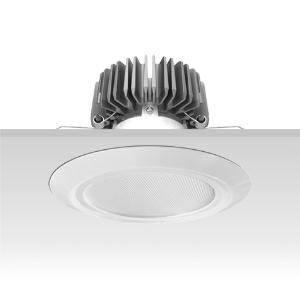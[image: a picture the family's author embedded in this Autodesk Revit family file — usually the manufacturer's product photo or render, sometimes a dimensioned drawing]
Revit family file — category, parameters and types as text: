
# Revit family: 3f_filippi_-_3f_reno_bianco_ampio_3f_filippi_-_30683_a01048_-_3f_reno_200_wh_3000-930_dali_wide___smp_wh_9ca3
name_source: partatom
category: Lighting Fixtures
units: mm (PartAtom-declared; Revit-internal decimal feet)

## family parameters
Cut with Voids When Loaded = No
Host = Face
Light Source = No
Part Type = Normal
Room Calculation Point = No
Round Connector Dimension = Use Diameter
Shared = No

## types (1)
- 3F Filippi - 3F Reno Bianco Ampio (1 x LED, 2320 lm, 37 W, 3000 K)
    Apparent Load = 37 VA
    Approval mark = CE
    CIE Flux Codes = 74 92 98 100 100
    Color Rendering = 90
    Color Temperature = 3000 K
    Control Gear = Electronic transformer
    Default Elevation = 1800 mm
    Description = ILLUMINOTECHNICAL
Luminous efficiency 100% (DLOR 100%, ULOR 0%).
Initial luminous flux of the luminaire 2320 lm.
Direct symmetric wide distribution.
Installation Interdistance Transv.D = 1.06 x hu - Long.D = 1.04 x hu.
Tabular UGR (CIE 117 - 4H-8H; S=0.25H; 70/50/20): RUG 22.5 - 22.3.
Beam angle: 70° - 69°.
Luminous efficacy 63 lm/W.
Lifetime (L90/B10): 30000 h. (tq+25°C)
Lifetime (L85/B10): 50000 h. (tq+25°C)
Lifetime (L70/B10): 80000 h. (tq+25°C)
Sudden decreased luminous flux after 50000 hours: 0% (C0).
Photobiological safety in compliance with IEC/TR 62778: RG0 risk exempt, (IEC 62471).
In compliance with IEC/EN 62722-2-1 - IEC/EN 62717 standards.

SOURCE
Compact LED module 3000/930.
Energy efficiency class (UE 2019/2020 - UE 2019/2015): E.
CIE 13.3 Colour rendering index: CRI >90 (R9 >50%).
IES TM-30 Fidelity Index: Rf = 92 Rg = 101.
CCT nominal colour temperature 3000 K.
Colour initial tolerance (MacAdam): SDCM 3.
Zhaga Book 3 compliant.

MECHANICAL
Passive heat dissipator in die-casting aluminium, oversized, for optimum thermal management of the LED module.
Parabolic element with graduated/concentric rings in white polycarbonate.
Transparent external lens with glossy and satin differentiated surfaces, with a cooling and anti-insect system in methacrylate (PMMA).
Fastening spring clips in stainless steel.
Dimensions: diameter 226 mm, height 146 mm. Weight 1.695 kg.
IP44 protection degree for exposed part, IP20 for recessed part.
Mechanical strength to impacts IK05 (0.7 joule).
Glow-wire test resistance 650°C.

ELECTRICAL
Wiring on a separate unit.
Halogen Free DALI-2 DATI (Parts 251, 252, 253), PUSH-DIM, electronic wiring 230V-50/60Hz, power factor 0.97 at full load, THD <25%, constant output current, SELV, class II, 1 driver, 1 DALI addresse.
Power of the luminaire 37 W.
ENEC - CE.
SAFE FLICKER: PstLM=<1 and SVM=<0.4 (IEC TR 61547-1 and IEC TR 63158), to ensure a more comfortable and safe light.
Luminaire compliant with EN 60598-2-22 for power supply from a centralised emergency system CPSS (Central Power Supply System), not incorporated in the luminaire - high risk areas excluded. The default power and flux are 100% in AC and 100% in DC.
Ambient temperature from 0°C to +25°C.
Temperature class T6 max 85°C.
Relative humidity UR: <85%.

INSTALLATION
Pull-up recessed fitting.
False ceiling carving: 200 mm.
All accessories dedicated to this product are available on the Catalog and on our website www.3F-Filippi.com.

ACCESSORIES
A01048 - Anti-glare microprismatic SMP diffuser in methacrylate (PMMA), locked and in line with the trim, in white polycarbonate.

APPLICATIONS
Suitable product for food production plants (HACCP), IFS (Food Version 6), BRC (GSFS Food Version 7).
Environments: architectural, commercial, exhibition areas, transit areas, corridors, shops, display windows, service areas.
In false ceilings with narrow voids.

LIGHT MANAGEMENT
Recommended minimum setting: 10%.
The luminaire, equipped with (DALI-2 DATI) driver, can be controlled manually with 3F Easy Dim technology or automatically/manually with wired or wireless DALI/D2D control systems.
The D2D driver guarantees interoperability with other devices with the same certification by making the following information available:
Device Data (Part 251), Energy Report (Part 252), Diagnosis & Maintenance (Part 253).
In electrical systems without a regulation system (manual or automatic) and DALI bus, a suitable jumper must be made on the DA-DA terminals of the appliance.

WARNING
Luminaire designed for disposal/recycling at end-of-life.
Replaceable (LED only) light source by a professional. Replaceable control gear by a professional.
    Height = 0 mm  [stored 0 ft]
    Lamp = 1 x LED
    Lamp Light Flux = 2320 lm
    Lamp Power = 37 W
    Lamp count = 1
    Length = 226 mm
    Lifetime = 50000 h
    Luminous efficacy = 63 lm/W
    Manufacturer = 3F Filippi
    ModVariant = No
    Model = 3F Filippi - 30683+A01048 - 3F Reno 200 WH 3000-930 DALI WIDE + SMP WH
    Mounting Place = Ceiling
    Mounting Type = Recessed
    Number of Poles = 1
    OnlyDefault = Yes
    Power Factor = 1
    Product Name = 3F Filippi - 3F Reno Bianco Ampio
    Product group = recessed luminaire
    ProductGroupID = 4
    Protection Class = Protection class II
    Protection Degree = IP 20
    RLX_Detail_Level = 1
    RLX_Emergency_Light_Flux = 0 lm
    RLX_Emergency_Type = 0
    RLX_Emergency_Type_DB = No
    RlxData = <blob elided: 96257 chars, md5=2801af51>
    Socket = socket
    Standby Power = 0 W
    System Light Flux = 2320 lm
    System Power = 37 W
    Type Comments = Product without accessories
    Type Image = 3ffilippi_3f_reno_200_wh_vs_smp.jpg
    URL = http://relux.com
    VarID = ---
    Voltage = 0 V
    Weight = 0.00 kg
    Width = 0 mm  [stored 0 ft]

note: [stored X ft] marks values corroborated as IEEE doubles in the binary element streams (Revit-internal decimal feet)

## geometry (parser evidence)
native form markers: Blend x4, Sweep x10
no freeform markers — native parametric forms only
